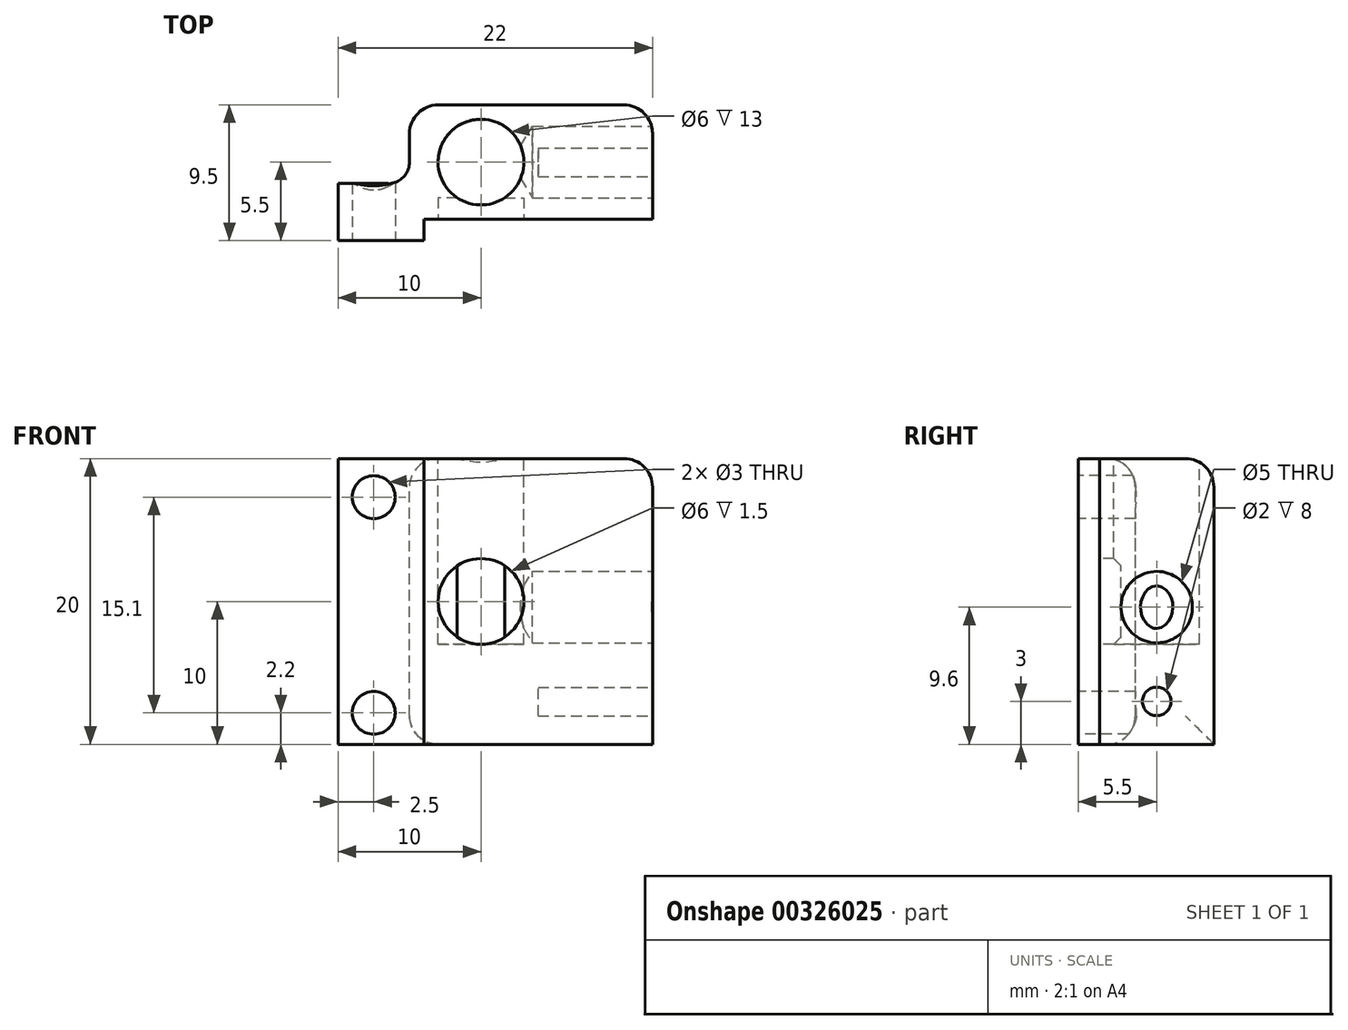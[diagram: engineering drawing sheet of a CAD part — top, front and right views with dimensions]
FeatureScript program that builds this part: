
annotation { "Feature Type Name" : "Feature", "Feature Type Description" : "" }
export const myFeature = defineFeature(function(context is Context, id is Id, definition is map)
    precondition{}
    {
        {
            var Q0;
            Q0=qCreatedBy(makeId("Top.planeOp"),FACE);
            var sketch = newSketch(context, id + "F0", { "sketchPlane" : qUnion([Q0])});
            skCircle(sketch, "E0", {"center": v(0, 0) * mm, "radius": 3 * mm});
            skLineSegment(sketch, "E1.bottom", {"start": v(-5, 4) * mm, "end": v(12, 4) * mm});
            skLineSegment(sketch, "E1.top", {"start": v(-4, -4) * mm, "end": v(12, -4) * mm});
            skLineSegment(sketch, "E1.left", {"start": v(-5, 4) * mm, "end": v(-5, 0) * mm});
            skLineSegment(sketch, "E1.right", {"start": v(12, 4) * mm, "end": v(12, -4) * mm});
            skLineSegment(sketch, "E2.bottom", {"start": v(-4, -5.5) * mm, "end": v(-10, -5.5) * mm});
            skLineSegment(sketch, "E2.top", {"start": v(-6.5, -1.5) * mm, "end": v(-10, -1.5) * mm});
            skLineSegment(sketch, "E2.left", {"start": v(-4, -5.5) * mm, "end": v(-4, -4) * mm});
            skLineSegment(sketch, "E2.right", {"start": v(-10, -5.5) * mm, "end": v(-10, -1.5) * mm});
            skLineSegment(sketch, "E3", {"start": v(-10, -1.5) * mm, "end": v(-10, 7.73) * mm, "construction": true});
            skLineSegment(sketch, "E4", {"start": v(-5, 4) * mm, "end": v(-14.37, 4) * mm, "construction": true});
            skArc(sketch, "E5", {"start": v(-6.5, -1.5) * mm, "mid": v(-5.44, -1.06) * mm, "end": v(-5, 0) * mm});
            skSolve(sketch);
        }
        {
            var Q0;
            Q0=makeQuery(id+"F0.imprint","IMPRINT",FACE,{"disambiguationData":[TD([[makeQuery(id+"F0.imprint","IMPRINT",EDGE,{"derivedFrom":sQuery(id+"F0.wireOp",EDGE,"E0")}),-1.0]])]});
            var Q1;
            Q1=makeQuery(id+"F0.imprint","IMPRINT",FACE,{"disambiguationData":[TD([[makeQuery(id+"F0.imprint","IMPRINT",EDGE,{"derivedFrom":sQuery(id+"F0.wireOp",EDGE,"E0")}),1.0]])]});
            extrude(context, id + "F1", {"entities" : qUnion([Q0, Q1]), "oppositeDirection" : true, "depth" : 7 * mm, "hasSecondDirection" : true, "secondDirectionOppositeDirection" : false, "secondDirectionDepth" : 13 * mm});
        }
        {
            var Q0;
            Q0=makeQuery(id+"F1.opExtrude","CAP_FACE",FACE,{"disambiguationData":[OSD([sQuery(id+"F0.wireOp",EDGE,"E1.bottom"),sQuery(id+"F0.wireOp",EDGE,"E1.top"),sQuery(id+"F0.wireOp",EDGE,"E1.left"),sQuery(id+"F0.wireOp",EDGE,"E1.right"),sQuery(id+"F0.wireOp",EDGE,"E2.bottom"),sQuery(id+"F0.wireOp",EDGE,"E2.top"),sQuery(id+"F0.wireOp",EDGE,"E2.left"),sQuery(id+"F0.wireOp",EDGE,"E2.right"),sQuery(id+"F0.wireOp",EDGE,"E5")])],"isStart":true});
            var sketch = newSketch(context, id + "F2", { "sketchPlane" : qUnion([Q0])});
            skCircle(sketch, "E6", {"center": v(0, 0) * mm, "radius": 3 * mm});
            skSolve(sketch);
        }
        {
            var Q0;
            Q0 = qSketchRegion(id + "F2", true);
            extrude(context, id + "F3", {"entities" : qUnion([Q0]), "operationType" : NewBodyOperationType.REMOVE, "oppositeDirection" : true, "depth" : 13 * mm});
        }
        {
            var Q0;
            Q0=makeQuery(id+"F1.opExtrude","SWEPT_FACE",FACE,{"disambiguationData":[OSD([sQuery(id+"F0.wireOp",EDGE,"E1.top")])]});
            var sketch = newSketch(context, id + "F4", { "sketchPlane" : qUnion([Q0])});
            skCircle(sketch, "E7", {"center": v(0, 3) * mm, "radius": 3 * mm});
            skSolve(sketch);
        }
        {
            var Q0;
            Q0=makeQuery(id+"F4.imprint","IMPRINT",FACE,{"disambiguationData":[TD([[makeQuery(id+"F4.imprint","IMPRINT",EDGE,{"derivedFrom":sQuery(id+"F4.wireOp",EDGE,"E7")}),1.0]])]});
            extrude(context, id + "F5", {"entities" : qUnion([Q0]), "operationType" : NewBodyOperationType.REMOVE, "oppositeDirection" : true, "depth" : 1.5 * mm});
        }
        {
            var Q0;
            Q0=makeQuery(id+"F1.opExtrude","SWEPT_FACE",FACE,{"disambiguationData":[OSD([sQuery(id+"F0.wireOp",EDGE,"E1.right")])]});
            var sketch = newSketch(context, id + "F6", { "sketchPlane" : qUnion([Q0])});
            skCircle(sketch, "E8", {"center": v(0, 2.6) * mm, "radius": 2.6 * mm});
            skSolve(sketch);
        }
        {
            var Q0;
            Q0=sQuery(id+"F6.wireOp",VERTEX,"E8.center");
            var Q1;
            Q1=makeQuery(id+"F1.opExtrude","SWEPT_BODY",BODY,{"disambiguationData":[OSD([sQuery(id+"F0.wireOp",EDGE,"E1.bottom"),sQuery(id+"F0.wireOp",EDGE,"E1.top"),sQuery(id+"F0.wireOp",EDGE,"E1.left"),sQuery(id+"F0.wireOp",EDGE,"E1.right"),sQuery(id+"F0.wireOp",EDGE,"E2.bottom"),sQuery(id+"F0.wireOp",EDGE,"E2.top"),sQuery(id+"F0.wireOp",EDGE,"E2.left"),sQuery(id+"F0.wireOp",EDGE,"E2.right"),sQuery(id+"F0.wireOp",EDGE,"E5")])]});
            hole(context, id + "F7", {"style" : HoleStyle.SIMPLE, "endStyle" : HoleEndStyle.BLIND, "holeDiameter" : 5 * mm, "holeDepth" : 8.4 * mm, "tappedDepth" : 12 * mm, "tapClearance" : 3, "locations" : qUnion([Q0]), "scope" : qUnion([Q1])});
        }
        {
            var Q0;
            Q0=makeQuery(id+"F1.opExtrude","SWEPT_FACE",FACE,{"disambiguationData":[OSD([sQuery(id+"F0.wireOp",EDGE,"E1.right")])]});
            var sketch = newSketch(context, id + "F8", { "sketchPlane" : qUnion([Q0])});
            skCircle(sketch, "E9", {"center": v(0, -4) * mm, "radius": 1 * mm});
            skSolve(sketch);
        }
        {
            var Q0;
            Q0=makeQuery(id+"F8.imprint","IMPRINT",FACE,{"disambiguationData":[TD([[makeQuery(id+"F8.imprint","IMPRINT",EDGE,{"derivedFrom":sQuery(id+"F8.wireOp",EDGE,"E9")}),1.0]])]});
            extrude(context, id + "F9", {"entities" : qUnion([Q0]), "operationType" : NewBodyOperationType.REMOVE, "oppositeDirection" : true, "depth" : 8 * mm});
        }
        {
            var Q0;
            Q0=makeQuery(id+"F1.opExtrude","SWEPT_FACE",FACE,{"disambiguationData":[OSD([sQuery(id+"F0.wireOp",EDGE,"E2.bottom")])]});
            var sketch = newSketch(context, id + "F10", { "sketchPlane" : qUnion([Q0])});
            skLineSegment(sketch, "E10", {"start": v(-7.5, 12.59) * mm, "end": v(-7.5, -7) * mm, "construction": true});
            skLineSegment(sketch, "E11", {"start": v(0, 13) * mm, "end": v(0, -7.6) * mm, "construction": true});
            skCircle(sketch, "E12", {"center": v(-7.5, 10.3) * mm, "radius": 1.5 * mm});
            skCircle(sketch, "E13", {"center": v(-7.5, -4.8) * mm, "radius": 1.5 * mm});
            skSolve(sketch);
        }
        {
            var Q0;
            Q0=makeQuery(id+"F10.imprint","IMPRINT",FACE,{"disambiguationData":[TD([[makeQuery(id+"F10.imprint","IMPRINT",EDGE,{"derivedFrom":sQuery(id+"F10.wireOp",EDGE,"E12")}),1.0]])]});
            var Q1;
            Q1=makeQuery(id+"F10.imprint","IMPRINT",FACE,{"disambiguationData":[TD([[makeQuery(id+"F10.imprint","IMPRINT",EDGE,{"derivedFrom":sQuery(id+"F10.wireOp",EDGE,"E13")}),1.0]])]});
            extrude(context, id + "F11", {"entities" : qUnion([Q0, Q1]), "operationType" : NewBodyOperationType.REMOVE, "oppositeDirection" : true, "depth" : 5 * mm});
        }
        {
            var Q0;
            Q0=makeQuery(id+"F1.opExtrude","CAP_EDGE",EDGE,{"disambiguationData":[OSD([sQuery(id+"F0.wireOp",EDGE,"E1.bottom")])],"isStart":true});
            var Q1;
            Q1=makeQuery(id+"F1.opExtrude","CAP_EDGE",EDGE,{"disambiguationData":[OSD([sQuery(id+"F0.wireOp",EDGE,"E1.left")])],"isStart":true});
            var Q2;
            Q2=makeQuery(id+"F1.opExtrude","CAP_EDGE",EDGE,{"disambiguationData":[OSD([sQuery(id+"F0.wireOp",EDGE,"E1.left")])],"isStart":false});
            var Q3;
            Q3=makeQuery(id+"F1.opExtrude","SWEPT_EDGE",EDGE,{"disambiguationData":[OSD([sQuery(id+"F0.wireOp",EDGE,"E1.bottom"),sQuery(id+"F0.wireOp",EDGE,"E1.left")])]});
            var Q4;
            Q4=makeQuery(id+"F1.opExtrude","SWEPT_EDGE",EDGE,{"disambiguationData":[OSD([sQuery(id+"F0.wireOp",EDGE,"E1.bottom"),sQuery(id+"F0.wireOp",EDGE,"E1.right")])]});
            var Q5;
            Q5=makeQuery(id+"F1.opExtrude","CAP_EDGE",EDGE,{"disambiguationData":[OSD([sQuery(id+"F0.wireOp",EDGE,"E1.right")])],"isStart":true});
            fillet(context, id + "F12", {"entities" : qUnion([Q0, Q1, Q2, Q3, Q4, Q5]), "radius" : 2 * mm, "tangentPropagation" : true, "allowEdgeOverflow" : false});
        }
    });
